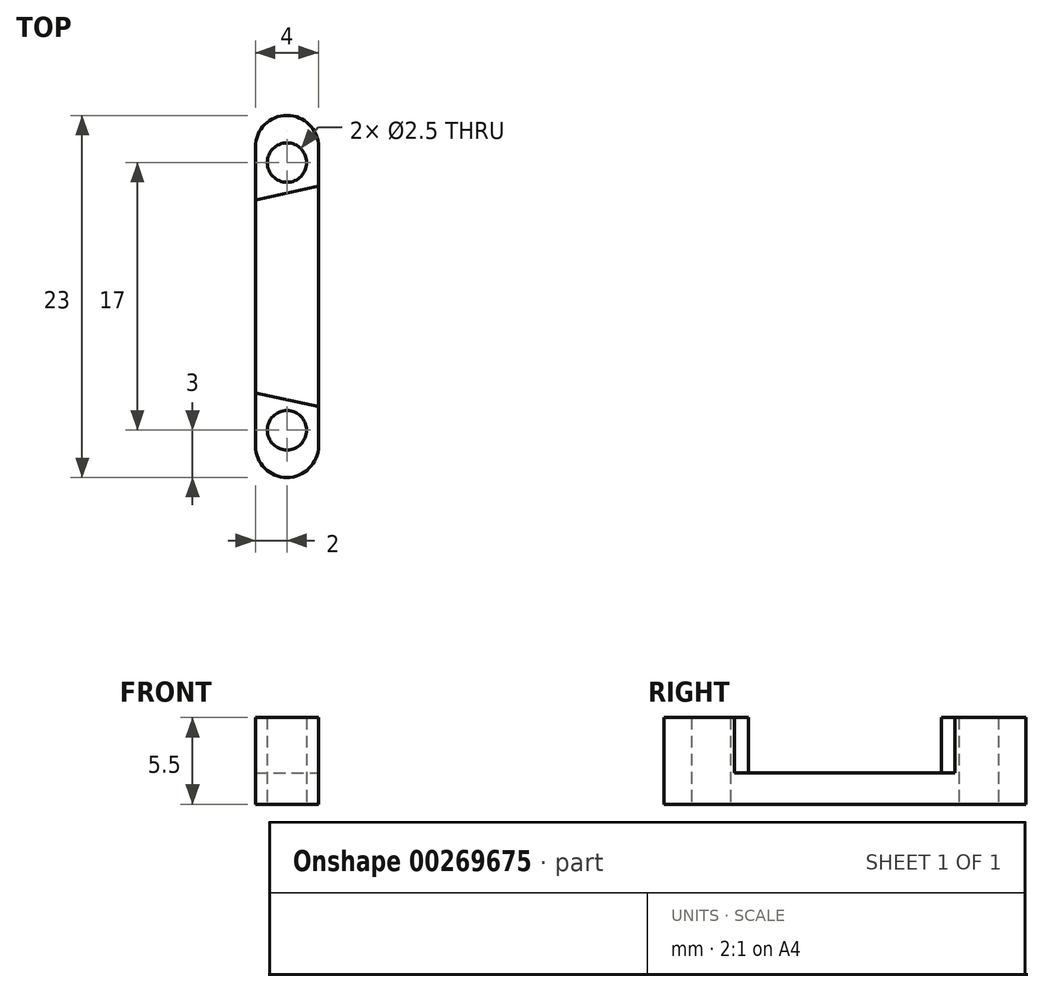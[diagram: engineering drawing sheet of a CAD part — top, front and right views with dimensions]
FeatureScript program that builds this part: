
annotation { "Feature Type Name" : "Feature", "Feature Type Description" : "" }
export const myFeature = defineFeature(function(context is Context, id is Id, definition is map)
    precondition{}
    {
        {
            var Q0;
            Q0=qCreatedBy(makeId("Top.planeOp"),FACE);
            var sketch = newSketch(context, id + "F0", { "sketchPlane" : qUnion([Q0])});
            skLineSegment(sketch, "E0.bottom", {"start": v(2, -11.5) * mm, "end": v(-2, -11.5) * mm});
            skLineSegment(sketch, "E0.top", {"start": v(2, 11.5) * mm, "end": v(-2, 11.5) * mm});
            skLineSegment(sketch, "E0.left", {"start": v(2, -11.5) * mm, "end": v(2, 11.5) * mm});
            skLineSegment(sketch, "E0.right", {"start": v(-2, -11.5) * mm, "end": v(-2, 11.5) * mm});
            skPoint(sketch, "E0.middle", {"position": v(0, 0) * mm});
            skCircle(sketch, "E1", {"center": v(0, 8.5) * mm, "radius": 1.25 * mm});
            skCircle(sketch, "E2.MirrorC", {"center": v(0, -8.5) * mm, "radius": 1.25 * mm});
            skLineSegment(sketch, "E3", {"start": v(-2, 6.13) * mm, "end": v(2, 7) * mm});
            skLineSegment(sketch, "E4.MirrorCS", {"start": v(-2, -6.13) * mm, "end": v(2, -7) * mm});
            skLineSegment(sketch, "E5.left", {"start": v(2, -8.2) * mm, "end": v(2, -11.5) * mm});
            skSolve(sketch);
        }
        {
            var Q0;
            {var subQ0=sQuery(id+"F0.wireOp",EDGE,"E3");Q0=makeQuery(id+"F0.imprint","IMPRINT",FACE,{"disambiguationData":[TD([[makeQuery(id+"F0.imprint","IMPRINT",EDGE,{"derivedFrom":subQ0}),-1.0]])]});}
            var Q1;
            {var subQ0=sQuery(id+"F0.wireOp",EDGE,"67ee3cb4-156f-4ee0-b22b-8525cf9fcae3");Q1=makeQuery(id+"F0.imprint","IMPRINT",FACE,{"disambiguationData":[TD([[makeQuery(id+"F0.imprint","IMPRINT",EDGE,{"derivedFrom":subQ0}),-1.0]])]});}
            var Q2;
            {var subQ0=sQuery(id+"F0.wireOp",EDGE,"e9c6fbd4-7eda-4daf-83b1-8ad9ca4f29a9");Q2=makeQuery(id+"F0.imprint","IMPRINT",FACE,{"disambiguationData":[TD([[makeQuery(id+"F0.imprint","IMPRINT",EDGE,{"derivedFrom":subQ0}),-1.0]])]});}
            var Q3;
            {var subQ0=sQuery(id+"F0.wireOp",EDGE,"61bac3ff-ae99-442a-a660-566b87a2d7c8");Q3=makeQuery(id+"F0.imprint","IMPRINT",FACE,{"disambiguationData":[TD([[makeQuery(id+"F0.imprint","IMPRINT",EDGE,{"derivedFrom":subQ0}),-1.0]])]});}
            extrude(context, id + "F1", {"entities" : qUnion([Q0, Q1, Q2, Q3]), "depth" : 2 * mm});
        }
        {
            var Q0;
            {var subQ0=sQuery(id+"F0.wireOp",EDGE,"E0.top");Q0=makeQuery(id+"F0.imprint","IMPRINT",FACE,{"disambiguationData":[TD([[makeQuery(id+"F0.imprint","IMPRINT",EDGE,{"derivedFrom":subQ0}),1.0]])]});}
            var Q1;
            {var subQ1=sQuery(id+"F0.wireOp",EDGE,"E0.bottom");Q1=makeQuery(id+"F0.imprint","IMPRINT",FACE,{"disambiguationData":[TD([[makeQuery(id+"F0.imprint","IMPRINT",EDGE,{"derivedFrom":subQ1}),-1.0]])]});}
            var Q2;
            {var subQ1=sQuery(id+"F0.wireOp",EDGE,"3d22448e-ce2c-4a20-88aa-23f1bb03a7a6.top");Q2=makeQuery(id+"F0.imprint","IMPRINT",FACE,{"disambiguationData":[TD([[makeQuery(id+"F0.imprint","IMPRINT",EDGE,{"derivedFrom":subQ1}),1.0]])]});}
            var Q3;
            {var subQ1=sQuery(id+"F0.wireOp",EDGE,"bdec14e2-428b-4702-9f6c-44220d4d4618.top");Q3=makeQuery(id+"F0.imprint","IMPRINT",FACE,{"disambiguationData":[TD([[makeQuery(id+"F0.imprint","IMPRINT",EDGE,{"derivedFrom":subQ1}),1.0]])]});}
            var Q4;
            {var subQ1=sQuery(id+"F0.wireOp",EDGE,"ee1911ab-919f-4d7b-a120-c973d131bfa4.top");Q4=makeQuery(id+"F0.imprint","IMPRINT",FACE,{"disambiguationData":[TD([[makeQuery(id+"F0.imprint","IMPRINT",EDGE,{"derivedFrom":subQ1}),1.0]])]});}
            var Q5;
            {var subQ1=sQuery(id+"F0.wireOp",EDGE,"ee1911ab-919f-4d7b-a120-c973d131bfa4.bottom");Q5=makeQuery(id+"F0.imprint","IMPRINT",FACE,{"disambiguationData":[TD([[makeQuery(id+"F0.imprint","IMPRINT",EDGE,{"derivedFrom":subQ1}),-1.0]])]});}
            var Q6;
            Q6=makeQuery(id+"F0.imprint","IMPRINT",FACE,{"disambiguationData":[TD([[makeQuery(id+"F0.imprint","IMPRINT",EDGE,{"derivedFrom":sQuery(id+"F0.wireOp",EDGE,"bdec14e2-428b-4702-9f6c-44220d4d4618.bottom")}),-1.0]])]});
            var Q7;
            Q7=makeQuery(id+"F0.imprint","IMPRINT",FACE,{"disambiguationData":[TD([[makeQuery(id+"F0.imprint","IMPRINT",EDGE,{"derivedFrom":sQuery(id+"F0.wireOp",EDGE,"3d22448e-ce2c-4a20-88aa-23f1bb03a7a6.bottom")}),-1.0]])]});
            extrude(context, id + "F2", {"entities" : qUnion([Q0, Q1, Q2, Q3, Q4, Q5, Q6, Q7]), "operationType" : NewBodyOperationType.ADD, "depth" : 5.5 * mm});
        }
        {
            var Q0;
            Q0=makeQuery(id+"F2.opExtrude","SWEPT_EDGE",EDGE,{"disambiguationData":[OSD([sQuery(id+"F0.wireOp",EDGE,"E0.top"),sQuery(id+"F0.wireOp",EDGE,"E0.left")])]});
            var Q1;
            Q1=makeQuery(id+"F2.opExtrude","SWEPT_EDGE",EDGE,{"disambiguationData":[OSD([sQuery(id+"F0.wireOp",EDGE,"E0.top"),sQuery(id+"F0.wireOp",EDGE,"E0.right")])]});
            var Q2;
            Q2=makeQuery(id+"F2.opExtrude","SWEPT_EDGE",EDGE,{"disambiguationData":[OSD([sQuery(id+"F0.wireOp",EDGE,"E0.bottom"),sQuery(id+"F0.wireOp",EDGE,"E0.left")])]});
            var Q3;
            Q3=makeQuery(id+"F2.opExtrude","SWEPT_EDGE",EDGE,{"disambiguationData":[OSD([sQuery(id+"F0.wireOp",EDGE,"E0.bottom"),sQuery(id+"F0.wireOp",EDGE,"E0.right")])]});
            var Q4;
            Q4=makeQuery(id+"F2.opExtrude","SWEPT_EDGE",EDGE,{"disambiguationData":[OSD([sQuery(id+"F0.wireOp",EDGE,"3d22448e-ce2c-4a20-88aa-23f1bb03a7a6.left"),sQuery(id+"F0.wireOp",EDGE,"67ee3cb4-156f-4ee0-b22b-8525cf9fcae3")])]});
            var Q5;
            Q5=makeQuery(id+"F2.opExtrude","SWEPT_EDGE",EDGE,{"disambiguationData":[OSD([sQuery(id+"F0.wireOp",EDGE,"bdec14e2-428b-4702-9f6c-44220d4d4618.left"),sQuery(id+"F0.wireOp",EDGE,"e9c6fbd4-7eda-4daf-83b1-8ad9ca4f29a9")])]});
            var Q6;
            Q6=makeQuery(id+"F2.opExtrude","SWEPT_EDGE",EDGE,{"disambiguationData":[OSD([sQuery(id+"F0.wireOp",EDGE,"ee1911ab-919f-4d7b-a120-c973d131bfa4.left"),sQuery(id+"F0.wireOp",EDGE,"61bac3ff-ae99-442a-a660-566b87a2d7c8")])]});
            var Q7;
            Q7=makeQuery(id+"F2.opExtrude","SWEPT_EDGE",EDGE,{"disambiguationData":[OSD([sQuery(id+"F0.wireOp",EDGE,"ee1911ab-919f-4d7b-a120-c973d131bfa4.top"),sQuery(id+"F0.wireOp",EDGE,"ee1911ab-919f-4d7b-a120-c973d131bfa4.left")])]});
            var Q8;
            Q8=makeQuery(id+"F2.opExtrude","SWEPT_EDGE",EDGE,{"disambiguationData":[OSD([sQuery(id+"F0.wireOp",EDGE,"bdec14e2-428b-4702-9f6c-44220d4d4618.top"),sQuery(id+"F0.wireOp",EDGE,"bdec14e2-428b-4702-9f6c-44220d4d4618.left")])]});
            var Q9;
            Q9=makeQuery(id+"F2.opExtrude","SWEPT_EDGE",EDGE,{"disambiguationData":[OSD([sQuery(id+"F0.wireOp",EDGE,"3d22448e-ce2c-4a20-88aa-23f1bb03a7a6.top"),sQuery(id+"F0.wireOp",EDGE,"3d22448e-ce2c-4a20-88aa-23f1bb03a7a6.left")])]});
            var Q10;
            Q10=makeQuery(id+"F2.opExtrude","SWEPT_EDGE",EDGE,{"disambiguationData":[OSD([sQuery(id+"F0.wireOp",EDGE,"3d22448e-ce2c-4a20-88aa-23f1bb03a7a6.left"),sQuery(id+"F0.wireOp",EDGE,"8136ce27-fc12-4940-a5ac-ff5d946e8e27.MirrorCS")])]});
            var Q11;
            Q11=makeQuery(id+"F2.opExtrude","SWEPT_EDGE",EDGE,{"disambiguationData":[OSD([sQuery(id+"F0.wireOp",EDGE,"3d22448e-ce2c-4a20-88aa-23f1bb03a7a6.bottom"),sQuery(id+"F0.wireOp",EDGE,"ucG4HMZJ-y8OG-HikN-iQNG-xdaYE6xnpcpw.top"),sQuery(id+"F0.wireOp",EDGE,"ucG4HMZJ-y8OG-HikN-iQNG-xdaYE6xnpcpw.left")])]});
            var Q12;
            Q12=makeQuery(id+"F2.opExtrude","SWEPT_EDGE",EDGE,{"disambiguationData":[OSD([sQuery(id+"F0.wireOp",EDGE,"3d22448e-ce2c-4a20-88aa-23f1bb03a7a6.bottom"),sQuery(id+"F0.wireOp",EDGE,"E5.top"),sQuery(id+"F0.wireOp",EDGE,"E5.right")])]});
            var Q13;
            Q13=makeQuery(id+"F2.opExtrude","SWEPT_EDGE",EDGE,{"disambiguationData":[OSD([sQuery(id+"F0.wireOp",EDGE,"bdec14e2-428b-4702-9f6c-44220d4d4618.left"),sQuery(id+"F0.wireOp",EDGE,"8d374e82-8bc1-45f9-bd52-95d40293e8c5.MirrorCS")])]});
            var Q14;
            Q14=makeQuery(id+"F2.opExtrude","SWEPT_EDGE",EDGE,{"disambiguationData":[OSD([sQuery(id+"F0.wireOp",EDGE,"bdec14e2-428b-4702-9f6c-44220d4d4618.bottom"),sQuery(id+"F0.wireOp",EDGE,"bCWOYJBy-4xy8-dxmD-uhx8-4cxaAyyJVkkr.top"),sQuery(id+"F0.wireOp",EDGE,"bCWOYJBy-4xy8-dxmD-uhx8-4cxaAyyJVkkr.left")])]});
            var Q15;
            Q15=makeQuery(id+"F2.opExtrude","SWEPT_EDGE",EDGE,{"disambiguationData":[OSD([sQuery(id+"F0.wireOp",EDGE,"bdec14e2-428b-4702-9f6c-44220d4d4618.bottom"),sQuery(id+"F0.wireOp",EDGE,"ucG4HMZJ-y8OG-HikN-iQNG-xdaYE6xnpcpw.top"),sQuery(id+"F0.wireOp",EDGE,"ucG4HMZJ-y8OG-HikN-iQNG-xdaYE6xnpcpw.right")])]});
            var Q16;
            Q16=makeQuery(id+"F2.opExtrude","SWEPT_EDGE",EDGE,{"disambiguationData":[OSD([sQuery(id+"F0.wireOp",EDGE,"ee1911ab-919f-4d7b-a120-c973d131bfa4.bottom"),sQuery(id+"F0.wireOp",EDGE,"ee1911ab-919f-4d7b-a120-c973d131bfa4.left")])]});
            var Q17;
            Q17=makeQuery(id+"F2.opExtrude","SWEPT_EDGE",EDGE,{"disambiguationData":[OSD([sQuery(id+"F0.wireOp",EDGE,"ee1911ab-919f-4d7b-a120-c973d131bfa4.bottom"),sQuery(id+"F0.wireOp",EDGE,"bCWOYJBy-4xy8-dxmD-uhx8-4cxaAyyJVkkr.top"),sQuery(id+"F0.wireOp",EDGE,"bCWOYJBy-4xy8-dxmD-uhx8-4cxaAyyJVkkr.right")])]});
            var Q18;
            Q18=makeQuery(id+"F2.opExtrude","SWEPT_EDGE",EDGE,{"disambiguationData":[OSD([sQuery(id+"F0.wireOp",EDGE,"ee1911ab-919f-4d7b-a120-c973d131bfa4.left"),sQuery(id+"F0.wireOp",EDGE,"3adb0f12-15ce-42a6-b6e5-b0b4d7f8cc12.MirrorCS")])]});
            var Q19;
            Q19=makeQuery(id+"F2.opExtrude","SWEPT_EDGE",EDGE,{"disambiguationData":[OSD([sQuery(id+"F0.wireOp",EDGE,"ee1911ab-919f-4d7b-a120-c973d131bfa4.top"),sQuery(id+"F0.wireOp",EDGE,"ee1911ab-919f-4d7b-a120-c973d131bfa4.right")])]});
            var Q20;
            Q20=makeQuery(id+"F2.opExtrude","SWEPT_EDGE",EDGE,{"disambiguationData":[OSD([sQuery(id+"F0.wireOp",EDGE,"bdec14e2-428b-4702-9f6c-44220d4d4618.top"),sQuery(id+"F0.wireOp",EDGE,"bdec14e2-428b-4702-9f6c-44220d4d4618.right")])]});
            var Q21;
            Q21=makeQuery(id+"F2.opExtrude","SWEPT_EDGE",EDGE,{"disambiguationData":[OSD([sQuery(id+"F0.wireOp",EDGE,"3d22448e-ce2c-4a20-88aa-23f1bb03a7a6.top"),sQuery(id+"F0.wireOp",EDGE,"3d22448e-ce2c-4a20-88aa-23f1bb03a7a6.right")])]});
            var Q22;
            Q22=makeQuery(id+"F2.opExtrude","SWEPT_EDGE",EDGE,{"disambiguationData":[OSD([sQuery(id+"F0.wireOp",EDGE,"E0.bottom"),sQuery(id+"F0.wireOp",EDGE,"E5.top"),sQuery(id+"F0.wireOp",EDGE,"E5.left")])]});
            fillet(context, id + "F3", {"entities" : qUnion([Q0, Q1, Q2, Q3, Q4, Q5, Q6, Q7, Q8, Q9, Q10, Q11, Q12, Q13, Q14, Q15, Q16, Q17, Q18, Q19, Q20, Q21, Q22]), "radius" : 2 * mm, "tangentPropagation" : true, "allowEdgeOverflow" : false});
        }
    });
